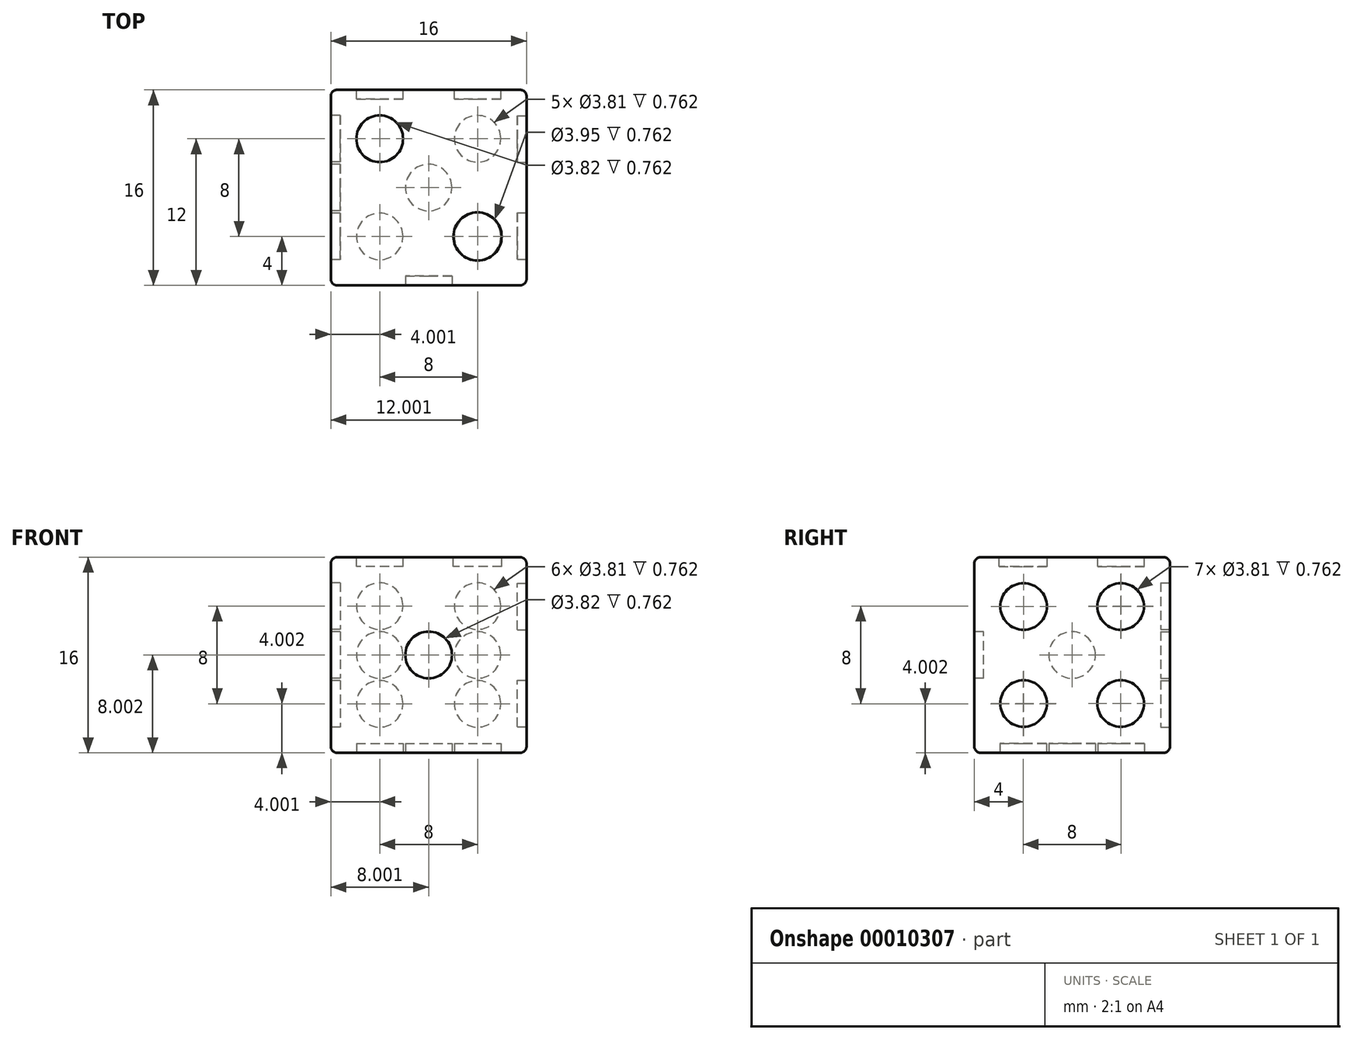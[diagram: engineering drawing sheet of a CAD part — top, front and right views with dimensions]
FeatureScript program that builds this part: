
annotation { "Feature Type Name" : "Feature", "Feature Type Description" : "" }
export const myFeature = defineFeature(function(context is Context, id is Id, definition is map)
    precondition{}
    {
        {
            var Q0;
            Q0=qCreatedBy(makeId("Front.planeOp"),FACE);
            var sketch = newSketch(context, id + "F0", { "sketchPlane" : qUnion([Q0])});
            skLineSegment(sketch, "E0.bottom", {"start": v(-181.29, -183.85) * mm, "end": v(-165.29, -183.85) * mm});
            skLineSegment(sketch, "E0.top", {"start": v(-181.29, -199.85) * mm, "end": v(-165.29, -199.85) * mm});
            skLineSegment(sketch, "E0.left", {"start": v(-181.29, -183.85) * mm, "end": v(-181.29, -199.85) * mm});
            skLineSegment(sketch, "E0.right", {"start": v(-165.29, -183.85) * mm, "end": v(-165.29, -199.85) * mm});
            skSolve(sketch);
        }
        {
            var Q0;
            Q0=makeQuery(id+"F0.imprint","IMPRINT",FACE,{"disambiguationData":[TD([[makeQuery(id+"F0.imprint","IMPRINT",EDGE,{"derivedFrom":sQuery(id+"F0.wireOp",EDGE,"E0.bottom")}),-1.0]])]});
            extrude(context, id + "F1", {"entities" : qUnion([Q0]), "depth" : 16 * mm});
        }
        {
            var Q0;
            Q0=makeQuery(id+"F1.opExtrude","CAP_FACE",FACE,{"disambiguationData":[OSD([sQuery(id+"F0.wireOp",EDGE,"E0.bottom"),sQuery(id+"F0.wireOp",EDGE,"E0.top"),sQuery(id+"F0.wireOp",EDGE,"E0.left"),sQuery(id+"F0.wireOp",EDGE,"E0.right")])],"isStart":false});
            var sketch = newSketch(context, id + "F2", { "sketchPlane" : qUnion([Q0])});
            skCircle(sketch, "E1", {"center": v(-173.29, -191.85) * mm, "radius": 1.9 * mm});
            skPoint(sketch, "E2", {"position": v(-173.42, -189.94) * mm});
            skSolve(sketch);
        }
        {
            var Q0;
            Q0=makeQuery(id+"F2.imprint","IMPRINT",FACE,{"disambiguationData":[TD([[makeQuery(id+"F2.imprint","IMPRINT",EDGE,{"derivedFrom":sQuery(id+"F2.wireOp",EDGE,"E1")}),1.0]])]});
            extrude(context, id + "F3", {"entities" : qUnion([Q0]), "operationType" : NewBodyOperationType.REMOVE, "oppositeDirection" : true, "depth" : 0.76 * mm});
        }
        {
            var Q0;
            Q0=makeQuery(id+"F1.opExtrude","SWEPT_FACE",FACE,{"disambiguationData":[OSD([sQuery(id+"F0.wireOp",EDGE,"E0.bottom")])]});
            var sketch = newSketch(context, id + "F4", { "sketchPlane" : qUnion([Q0])});
            skCircle(sketch, "E3", {"center": v(-177.29, -4) * mm, "radius": 1.9 * mm});
            skPoint(sketch, "E4", {"position": v(-175.38, -3.89) * mm});
            skCircle(sketch, "E5", {"center": v(-169.29, -12) * mm, "radius": 1.97 * mm});
            skPoint(sketch, "E6", {"position": v(-167.34, -11.7) * mm});
            skPoint(sketch, "E7", {"position": v(-167.38, -11.68) * mm});
            skSolve(sketch);
        }
        {
            var Q0;
            Q0=makeQuery(id+"F1.opExtrude","SWEPT_FACE",FACE,{"disambiguationData":[OSD([sQuery(id+"F0.wireOp",EDGE,"E0.left")])]});
            var sketch = newSketch(context, id + "F5", { "sketchPlane" : qUnion([Q0])});
            skCircle(sketch, "E8", {"center": v(8, -191.85) * mm, "radius": 1.9 * mm});
            skCircle(sketch, "E9", {"center": v(4, -187.85) * mm, "radius": 1.9 * mm});
            skCircle(sketch, "E10", {"center": v(12, -195.85) * mm, "radius": 1.9 * mm});
            skPoint(sketch, "E11", {"position": v(5.9, -187.89) * mm});
            skPoint(sketch, "E12", {"position": v(9.86, -191.42) * mm});
            skPoint(sketch, "E13", {"position": v(12.31, -193.97) * mm});
            skSolve(sketch);
        }
        {
            var Q0;
            Q0=makeQuery(id+"F1.opExtrude","CAP_FACE",FACE,{"disambiguationData":[OSD([sQuery(id+"F0.wireOp",EDGE,"E0.bottom"),sQuery(id+"F0.wireOp",EDGE,"E0.top"),sQuery(id+"F0.wireOp",EDGE,"E0.left"),sQuery(id+"F0.wireOp",EDGE,"E0.right")])],"isStart":true});
            var sketch = newSketch(context, id + "F6", { "sketchPlane" : qUnion([Q0])});
            skLineSegment(sketch, "E14", {"start": v(173.29, -183.85) * mm, "end": v(165.29, -183.85) * mm});
            skLineSegment(sketch, "E15", {"start": v(173.29, -183.85) * mm, "end": v(181.29, -183.85) * mm});
            skLineSegment(sketch, "E16", {"start": v(165.29, -191.85) * mm, "end": v(165.29, -183.85) * mm});
            skLineSegment(sketch, "E17", {"start": v(165.29, -191.85) * mm, "end": v(165.29, -199.85) * mm});
            skCircle(sketch, "E18", {"center": v(169.29, -187.85) * mm, "radius": 1.9 * mm});
            skCircle(sketch, "E19", {"center": v(169.29, -191.85) * mm, "radius": 1.9 * mm});
            skCircle(sketch, "E20", {"center": v(169.29, -195.85) * mm, "radius": 1.9 * mm});
            skCircle(sketch, "E21", {"center": v(177.29, -187.85) * mm, "radius": 1.9 * mm});
            skCircle(sketch, "E22", {"center": v(177.29, -191.85) * mm, "radius": 1.9 * mm});
            skCircle(sketch, "E23", {"center": v(177.29, -195.85) * mm, "radius": 1.9 * mm});
            skPoint(sketch, "E24", {"position": v(170.47, -186.35) * mm});
            skPoint(sketch, "E25", {"position": v(170.84, -190.74) * mm});
            skPoint(sketch, "E26", {"position": v(170.83, -194.73) * mm});
            skPoint(sketch, "E27", {"position": v(178.86, -186.77) * mm});
            skPoint(sketch, "E28", {"position": v(178.55, -190.42) * mm});
            skPoint(sketch, "E29", {"position": v(177.98, -194.07) * mm});
            skSolve(sketch);
        }
        {
            var Q0;
            Q0=makeQuery(id+"F1.opExtrude","SWEPT_FACE",FACE,{"disambiguationData":[OSD([sQuery(id+"F0.wireOp",EDGE,"E0.top")])]});
            var sketch = newSketch(context, id + "F7", { "sketchPlane" : qUnion([Q0])});
            skCircle(sketch, "E30", {"center": v(-169.29, 4) * mm, "radius": 1.9 * mm});
            skCircle(sketch, "E31", {"center": v(-173.29, 8) * mm, "radius": 1.9 * mm});
            skCircle(sketch, "E32", {"center": v(-177.29, 4) * mm, "radius": 1.9 * mm});
            skCircle(sketch, "E33", {"center": v(-169.29, 12) * mm, "radius": 1.9 * mm});
            skCircle(sketch, "E34", {"center": v(-177.29, 12) * mm, "radius": 1.9 * mm});
            skPoint(sketch, "E35", {"position": v(-171.03, 3.24) * mm});
            skPoint(sketch, "E36", {"position": v(-175.5, 3.34) * mm});
            skPoint(sketch, "E37", {"position": v(-173.64, 6.13) * mm});
            skPoint(sketch, "E38", {"position": v(-175.56, 11.2) * mm});
            skPoint(sketch, "E39", {"position": v(-170.93, 11.04) * mm});
            skSolve(sketch);
        }
        {
            var Q0;
            Q0=makeQuery(id+"F1.opExtrude","SWEPT_FACE",FACE,{"disambiguationData":[OSD([sQuery(id+"F0.wireOp",EDGE,"E0.right")])]});
            var sketch = newSketch(context, id + "F8", { "sketchPlane" : qUnion([Q0])});
            skCircle(sketch, "E40", {"center": v(-4.02, -187.88) * mm, "radius": 1.9 * mm});
            skCircle(sketch, "E41", {"center": v(-11.97, -187.88) * mm, "radius": 1.9 * mm});
            skCircle(sketch, "E42", {"center": v(-11.97, -195.82) * mm, "radius": 1.9 * mm});
            skCircle(sketch, "E43", {"center": v(-4.02, -195.82) * mm, "radius": 1.9 * mm});
            skPoint(sketch, "E44", {"position": v(-2.14, -187.63) * mm});
            skPoint(sketch, "E45", {"position": v(-10.1, -188.26) * mm});
            skPoint(sketch, "E46", {"position": v(-2.18, -195.35) * mm});
            skPoint(sketch, "E47", {"position": v(-10.21, -196.57) * mm});
            skSolve(sketch);
        }
        {
            var Q0;
            Q0=makeQuery(id+"F4.imprint","IMPRINT",FACE,{"disambiguationData":[TD([[makeQuery(id+"F4.imprint","IMPRINT",EDGE,{"derivedFrom":sQuery(id+"F4.wireOp",EDGE,"E3")}),1.0]])]});
            var Q1;
            Q1=makeQuery(id+"F4.imprint","IMPRINT",FACE,{"disambiguationData":[TD([[makeQuery(id+"F4.imprint","IMPRINT",EDGE,{"derivedFrom":sQuery(id+"F4.wireOp",EDGE,"E5")}),1.0]])]});
            extrude(context, id + "F9", {"entities" : qUnion([Q0, Q1]), "operationType" : NewBodyOperationType.REMOVE, "oppositeDirection" : true, "depth" : 0.76 * mm});
        }
        {
            var Q0;
            Q0=makeQuery(id+"F8.imprint","IMPRINT",FACE,{"disambiguationData":[TD([[makeQuery(id+"F8.imprint","IMPRINT",EDGE,{"derivedFrom":sQuery(id+"F8.wireOp",EDGE,"E41")}),1.0]])]});
            var Q1;
            Q1=makeQuery(id+"F8.imprint","IMPRINT",FACE,{"disambiguationData":[TD([[makeQuery(id+"F8.imprint","IMPRINT",EDGE,{"derivedFrom":sQuery(id+"F8.wireOp",EDGE,"E40")}),1.0]])]});
            var Q2;
            Q2=makeQuery(id+"F8.imprint","IMPRINT",FACE,{"disambiguationData":[TD([[makeQuery(id+"F8.imprint","IMPRINT",EDGE,{"derivedFrom":sQuery(id+"F8.wireOp",EDGE,"E43")}),1.0]])]});
            var Q3;
            Q3=makeQuery(id+"F8.imprint","IMPRINT",FACE,{"disambiguationData":[TD([[makeQuery(id+"F8.imprint","IMPRINT",EDGE,{"derivedFrom":sQuery(id+"F8.wireOp",EDGE,"E42")}),1.0]])]});
            extrude(context, id + "F10", {"entities" : qUnion([Q0, Q1, Q2, Q3]), "operationType" : NewBodyOperationType.REMOVE, "oppositeDirection" : true, "depth" : 0.76 * mm});
        }
        {
            var Q0;
            Q0=makeQuery(id+"F6.imprint","IMPRINT",FACE,{"disambiguationData":[TD([[makeQuery(id+"F6.imprint","IMPRINT",EDGE,{"derivedFrom":sQuery(id+"F6.wireOp",EDGE,"E18")}),1.0]])]});
            var Q1;
            Q1=makeQuery(id+"F6.imprint","IMPRINT",FACE,{"disambiguationData":[TD([[makeQuery(id+"F6.imprint","IMPRINT",EDGE,{"derivedFrom":sQuery(id+"F6.wireOp",EDGE,"E19")}),1.0]])]});
            var Q2;
            Q2=makeQuery(id+"F6.imprint","IMPRINT",FACE,{"disambiguationData":[TD([[makeQuery(id+"F6.imprint","IMPRINT",EDGE,{"derivedFrom":sQuery(id+"F6.wireOp",EDGE,"E20")}),1.0]])]});
            var Q3;
            Q3=makeQuery(id+"F6.imprint","IMPRINT",FACE,{"disambiguationData":[TD([[makeQuery(id+"F6.imprint","IMPRINT",EDGE,{"derivedFrom":sQuery(id+"F6.wireOp",EDGE,"E21")}),1.0]])]});
            var Q4;
            Q4=makeQuery(id+"F6.imprint","IMPRINT",FACE,{"disambiguationData":[TD([[makeQuery(id+"F6.imprint","IMPRINT",EDGE,{"derivedFrom":sQuery(id+"F6.wireOp",EDGE,"E22")}),1.0]])]});
            var Q5;
            Q5=makeQuery(id+"F6.imprint","IMPRINT",FACE,{"disambiguationData":[TD([[makeQuery(id+"F6.imprint","IMPRINT",EDGE,{"derivedFrom":sQuery(id+"F6.wireOp",EDGE,"E23")}),1.0]])]});
            extrude(context, id + "F11", {"entities" : qUnion([Q0, Q1, Q2, Q3, Q4, Q5]), "operationType" : NewBodyOperationType.REMOVE, "oppositeDirection" : true, "depth" : 0.76 * mm});
        }
        {
            var Q0;
            Q0=makeQuery(id+"F7.imprint","IMPRINT",FACE,{"disambiguationData":[TD([[makeQuery(id+"F7.imprint","IMPRINT",EDGE,{"derivedFrom":sQuery(id+"F7.wireOp",EDGE,"E30")}),1.0]])]});
            var Q1;
            Q1=makeQuery(id+"F7.imprint","IMPRINT",FACE,{"disambiguationData":[TD([[makeQuery(id+"F7.imprint","IMPRINT",EDGE,{"derivedFrom":sQuery(id+"F7.wireOp",EDGE,"E32")}),1.0]])]});
            var Q2;
            Q2=makeQuery(id+"F7.imprint","IMPRINT",FACE,{"disambiguationData":[TD([[makeQuery(id+"F7.imprint","IMPRINT",EDGE,{"derivedFrom":sQuery(id+"F7.wireOp",EDGE,"E31")}),1.0]])]});
            var Q3;
            Q3=makeQuery(id+"F7.imprint","IMPRINT",FACE,{"disambiguationData":[TD([[makeQuery(id+"F7.imprint","IMPRINT",EDGE,{"derivedFrom":sQuery(id+"F7.wireOp",EDGE,"E33")}),1.0]])]});
            var Q4;
            Q4=makeQuery(id+"F7.imprint","IMPRINT",FACE,{"disambiguationData":[TD([[makeQuery(id+"F7.imprint","IMPRINT",EDGE,{"derivedFrom":sQuery(id+"F7.wireOp",EDGE,"E34")}),1.0]])]});
            extrude(context, id + "F12", {"entities" : qUnion([Q0, Q1, Q2, Q3, Q4]), "operationType" : NewBodyOperationType.REMOVE, "oppositeDirection" : true, "depth" : 0.76 * mm});
        }
        {
            var Q0;
            Q0=makeQuery(id+"F5.imprint","IMPRINT",FACE,{"disambiguationData":[TD([[makeQuery(id+"F5.imprint","IMPRINT",EDGE,{"derivedFrom":sQuery(id+"F5.wireOp",EDGE,"E10")}),1.0]])]});
            var Q1;
            Q1=makeQuery(id+"F5.imprint","IMPRINT",FACE,{"disambiguationData":[TD([[makeQuery(id+"F5.imprint","IMPRINT",EDGE,{"derivedFrom":sQuery(id+"F5.wireOp",EDGE,"E8")}),1.0]])]});
            var Q2;
            Q2=makeQuery(id+"F5.imprint","IMPRINT",FACE,{"disambiguationData":[TD([[makeQuery(id+"F5.imprint","IMPRINT",EDGE,{"derivedFrom":sQuery(id+"F5.wireOp",EDGE,"E9")}),1.0]])]});
            extrude(context, id + "F13", {"entities" : qUnion([Q0, Q1, Q2]), "operationType" : NewBodyOperationType.REMOVE, "oppositeDirection" : true, "depth" : 0.76 * mm});
        }
        {
            var Q0;
            Q0=makeQuery(id+"F1.opExtrude","CAP_EDGE",EDGE,{"disambiguationData":[OSD([sQuery(id+"F0.wireOp",EDGE,"E0.left")])],"isStart":false});
            var Q1;
            Q1=makeQuery(id+"F1.opExtrude","CAP_EDGE",EDGE,{"disambiguationData":[OSD([sQuery(id+"F0.wireOp",EDGE,"E0.bottom")])],"isStart":false});
            var Q2;
            Q2=makeQuery(id+"F1.opExtrude","SWEPT_EDGE",EDGE,{"disambiguationData":[OSD([sQuery(id+"F0.wireOp",EDGE,"E0.bottom"),sQuery(id+"F0.wireOp",EDGE,"E0.left")])]});
            var Q3;
            Q3=makeQuery(id+"F1.opExtrude","SWEPT_EDGE",EDGE,{"disambiguationData":[OSD([sQuery(id+"F0.wireOp",EDGE,"E0.bottom"),sQuery(id+"F0.wireOp",EDGE,"E0.right")])]});
            var Q4;
            Q4=makeQuery(id+"F1.opExtrude","SWEPT_EDGE",EDGE,{"disambiguationData":[OSD([sQuery(id+"F0.wireOp",EDGE,"E0.top"),sQuery(id+"F0.wireOp",EDGE,"E0.right")])]});
            var Q5;
            Q5=makeQuery(id+"F1.opExtrude","CAP_EDGE",EDGE,{"disambiguationData":[OSD([sQuery(id+"F0.wireOp",EDGE,"E0.top")])],"isStart":false});
            var Q6;
            Q6=makeQuery(id+"F1.opExtrude","CAP_EDGE",EDGE,{"disambiguationData":[OSD([sQuery(id+"F0.wireOp",EDGE,"E0.bottom")])],"isStart":true});
            var Q7;
            Q7=makeQuery(id+"F1.opExtrude","CAP_EDGE",EDGE,{"disambiguationData":[OSD([sQuery(id+"F0.wireOp",EDGE,"E0.right")])],"isStart":true});
            var Q8;
            Q8=makeQuery(id+"F1.opExtrude","CAP_EDGE",EDGE,{"disambiguationData":[OSD([sQuery(id+"F0.wireOp",EDGE,"E0.left")])],"isStart":true});
            var Q9;
            Q9=makeQuery(id+"F1.opExtrude","CAP_EDGE",EDGE,{"disambiguationData":[OSD([sQuery(id+"F0.wireOp",EDGE,"E0.top")])],"isStart":true});
            var Q10;
            Q10=makeQuery(id+"F1.opExtrude","SWEPT_EDGE",EDGE,{"disambiguationData":[OSD([sQuery(id+"F0.wireOp",EDGE,"E0.top"),sQuery(id+"F0.wireOp",EDGE,"E0.left")])]});
            var Q11;
            Q11=makeQuery(id+"F1.opExtrude","CAP_EDGE",EDGE,{"disambiguationData":[OSD([sQuery(id+"F0.wireOp",EDGE,"E0.right")])],"isStart":false});
            fillet(context, id + "F14", {"entities" : qUnion([Q0, Q1, Q2, Q3, Q4, Q5, Q6, Q7, Q8, Q9, Q10, Q11]), "radius" : 0.5 * mm, "tangentPropagation" : true, "allowEdgeOverflow" : false});
        }
    });
